# Revit family: spectral_iris_iris-e-led_4080-840-t
name_source: partatom
category: Lighting Fixtures
revit_build: Autodesk Revit 2016 (Build: 20150220_1215(x64)
units: mm (PartAtom-declared; Revit-internal decimal feet)

## family parameters
Cut with Voids When Loaded = No
Host = Face
Light Source = No
Part Type = Normal
Room Calculation Point = No
Round Connector Dimension = Use Diameter
Shared = No

## types (1)
- SPECTRAL IRIS (1 x )
    Apparent Load = 0 VA
    Approval mark = CE
    CIE Flux Codes = 70 91 98 100 59
    Control Gear = Electronic transformer
    Default Elevation = 1800 mm
    Description = SPI0000038AY
IRIS recessed luminaire

Design:
Ring-shaped recessed luminaire made of highly transparent plastic. The rotationally symmetrical, flame retardant and impact resistant luminaire housing is slightly offset within the recessed ceiling housing. Transparent insect protection ring separately available as an accessory. Glare reduction by means of round diffuser panel made of highly transparent plastic with microprism structure which clips in from below. Central round white powder-coated steel panel to cover the gear tray. Round recessed ceiling housing made of aluminium with specular surface serves as a large secondary reflective surface. Recessed ceiling housing is mounted using a cross-shaped mounting bracket. Ceiling luminaire with heat-resistant wiring. All metal parts are powder coated. 

Colour: housing – transparent; ceiling box similar to RAL 9016 White silk matt. Colour accentuation of the housing possible by inserting a separately available colour inlay film. 

LED: 3 LED ring segment boards for direct lighting component and 3 LED 
ring segment boards for indirect lighting component using the secondary
reflector. Light colours 830, 840.

Mounting dimensions: HU = 115 mm / DU = 485 mm

Safety class I
Protection rating IP20
    Height = 0 mm  [stored 0 ft]
    Lamp = 1 x
    Lamp count = 1
    Length = 520 mm
    Luminous efficacy = 0 lm/W
    Manufacturer = Ridi
    ModVariant = No
    Model = IRIS-E-LED 4080-840-T
    Mounting Place = Ceiling
    Mounting Type = Recessed
    Number of Poles = 1
    OnlyDefault = Yes
    Power Factor = 1
    Product Name = SPECTRAL IRIS
    Product group = Recessed luminaire
    ProductGroupID = 4
    Protection Class = Protection class
    Protection Degree = IP 20
    RlxData = <blob elided: 49141 chars, md5=c617724d>
    Socket = socket
    Standby Power = 0 W
    System Light Flux = 0 lm
    System Power = 0 W
    Type Image = 001_iri_deb_01700271_001.jpg
    URL = http://reluxnet.relux.com
    VarID = 1
    Voltage = 0 V
    Weight = 0.00 kg
    Width = 0 mm  [stored 0 ft]

note: [stored X ft] marks values corroborated as IEEE doubles in the binary element streams (Revit-internal decimal feet)

## geometry (parser evidence)
native form markers: Blend x4, Sweep x10
no freeform markers — native parametric forms only
